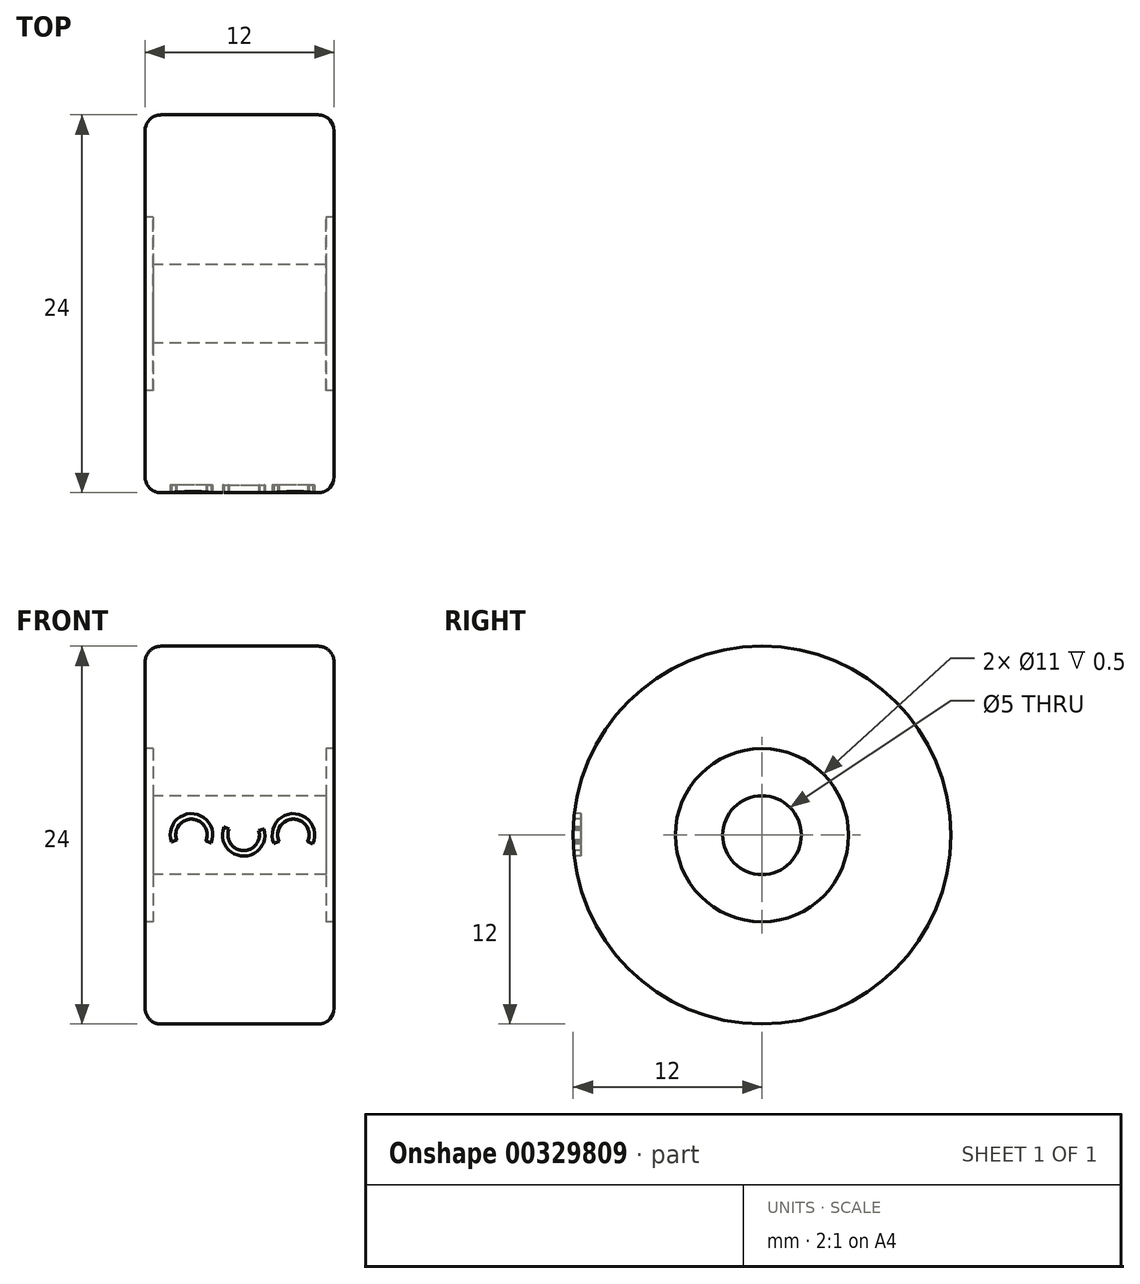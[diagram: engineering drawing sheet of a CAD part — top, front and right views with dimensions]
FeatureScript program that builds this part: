
annotation { "Feature Type Name" : "Feature", "Feature Type Description" : "" }
export const myFeature = defineFeature(function(context is Context, id is Id, definition is map)
    precondition{}
    {
        {
            var Q0;
            Q0=qCreatedBy(makeId("Top.planeOp"),FACE);
            var sketch = newSketch(context, id + "F0", { "sketchPlane" : qUnion([Q0])});
            skLineSegment(sketch, "E0.bottom", {"start": v(0, 0) * mm, "end": v(12, 0) * mm});
            skLineSegment(sketch, "E0.top", {"start": v(1, 12) * mm, "end": v(11, 12) * mm});
            skLineSegment(sketch, "E0.left", {"start": v(0, 0) * mm, "end": v(0, 11) * mm});
            skLineSegment(sketch, "E0.right", {"start": v(12, 0) * mm, "end": v(12, 11) * mm});
            skLineSegment(sketch, "E1", {"start": v(0, 2.5) * mm, "end": v(12, 2.5) * mm});
            skPoint(sketch, "E2.visualSharp", {"position": v(0, 12) * mm});
            skArc(sketch, "E2.filletArc", {"start": v(1, 12) * mm, "mid": v(0.3, 11.7) * mm, "end": v(0, 11) * mm});
            skPoint(sketch, "E3.visualSharp", {"position": v(12, 12) * mm});
            skArc(sketch, "E3.filletArc", {"start": v(12, 11) * mm, "mid": v(11.7, 11.7) * mm, "end": v(11, 12) * mm});
            skLineSegment(sketch, "E4", {"start": v(0, 5.5) * mm, "end": v(0.5, 5.5) * mm});
            skPoint(sketch, "E4.endSnap0", {"position": v(0, 5.5) * mm});
            skLineSegment(sketch, "E5", {"start": v(0.5, 5.5) * mm, "end": v(0.5, 2.5) * mm});
            skLineSegment(sketch, "E6", {"start": v(12, 5.5) * mm, "end": v(11.5, 5.5) * mm});
            skPoint(sketch, "E6.endSnap0", {"position": v(12, 5.5) * mm});
            skLineSegment(sketch, "E7", {"start": v(11.5, 5.5) * mm, "end": v(11.5, 2.5) * mm});
            skSolve(sketch);
        }
        {
            var Q0;
            Q0=makeQuery(id+"F0.imprint","IMPRINT",FACE,{"disambiguationData":[TD([[makeQuery(id+"F0.imprint","IMPRINT",EDGE,{"derivedFrom":sQuery(id+"F0.wireOp",EDGE,"E0.top")}),-1.0]])]});
            var Q1;
            Q1=sQuery(id+"F0.wireOp",EDGE,"E0.bottom");
            revolve(context, id + "F1", {"entities" : qUnion([Q0]), "axis" : qUnion([Q1]), "revolveType" : RevolveType.FULL});
        }
        {
            var Q0;
            Q0=qCreatedBy(makeId("Right.planeOp"),FACE);
            var sketch = newSketch(context, id + "F2", { "sketchPlane" : qUnion([Q0])});
            skLineSegment(sketch, "E8", {"start": v(0, 0) * mm, "end": v(-20.25, 1.77) * mm, "construction": true});
            skLineSegment(sketch, "E9", {"start": v(0, 0) * mm, "end": v(-21.92, -1.92) * mm, "construction": true});
            skSolve(sketch);
        }
        {
            var Q0;
            Q0=qCreatedBy(makeId("Front.planeOp"),FACE);
            cPlane(context, id + "F3", {"entities" : qUnion([Q0]), "cplaneType" : CPlaneType.OFFSET, "offset" : 12 * mm, "width" : 150 * mm, "height" : 150 * mm});
        }
        {
            var Q0;
            Q0=qCreatedBy(id+"F3.planeOp",FACE);
            var sketch = newSketch(context, id + "F4", { "sketchPlane" : qUnion([Q0])});
            skLineSegment(sketch, "E10.0", {"start": v(0, 0.02) * mm, "end": v(0, 1.79) * mm});
            skLineSegment(sketch, "E11.0", {"start": v(0, 0.02) * mm, "end": v(0, -1.9) * mm});
            skLineSegment(sketch, "E12", {"start": v(0, 1.79) * mm, "end": v(14.76, 1.79) * mm, "construction": true});
            skLineSegment(sketch, "E13", {"start": v(0, -1.9) * mm, "end": v(14.85, -1.9) * mm, "construction": true});
            skArc(sketch, "E14", {"start": v(3.87, -0.37) * mm, "mid": v(2.97, 1.02) * mm, "end": v(2, -0.31) * mm});
            skArc(sketch, "E15", {"start": v(4.19, -0.5) * mm, "mid": v(2.98, 1.37) * mm, "end": v(1.67, -0.43) * mm});
            skLineSegment(sketch, "E16", {"start": v(1.67, -0.43) * mm, "end": v(2, -0.31) * mm});
            skLineSegment(sketch, "E17", {"start": v(3.87, -0.37) * mm, "end": v(4.19, -0.5) * mm});
            skArc(sketch, "E18", {"start": v(5.33, 0.39) * mm, "mid": v(6.2, -0.98) * mm, "end": v(7.22, 0.3) * mm});
            skArc(sketch, "E19", {"start": v(5, 0.52) * mm, "mid": v(6.19, -1.33) * mm, "end": v(7.55, 0.39) * mm});
            skLineSegment(sketch, "E20", {"start": v(5, 0.52) * mm, "end": v(5.33, 0.39) * mm});
            skLineSegment(sketch, "E21", {"start": v(7.22, 0.3) * mm, "end": v(7.55, 0.39) * mm});
            skArc(sketch, "E22", {"start": v(10.32, -0.4) * mm, "mid": v(9.43, 1.02) * mm, "end": v(8.5, -0.39) * mm});
            skArc(sketch, "E23", {"start": v(10.64, -0.55) * mm, "mid": v(9.43, 1.37) * mm, "end": v(8.18, -0.53) * mm});
            skLineSegment(sketch, "E24", {"start": v(8.18, -0.53) * mm, "end": v(8.5, -0.39) * mm});
            skLineSegment(sketch, "E25", {"start": v(10.32, -0.4) * mm, "end": v(10.64, -0.55) * mm});
            skSolve(sketch);
        }
        {
            var Q0;
            Q0 = qSketchRegion(id + "F4", true);
            extrude(context, id + "F5", {"entities" : qUnion([Q0]), "operationType" : NewBodyOperationType.REMOVE, "oppositeDirection" : true, "depth" : 0.5 * mm});
        }
    });
